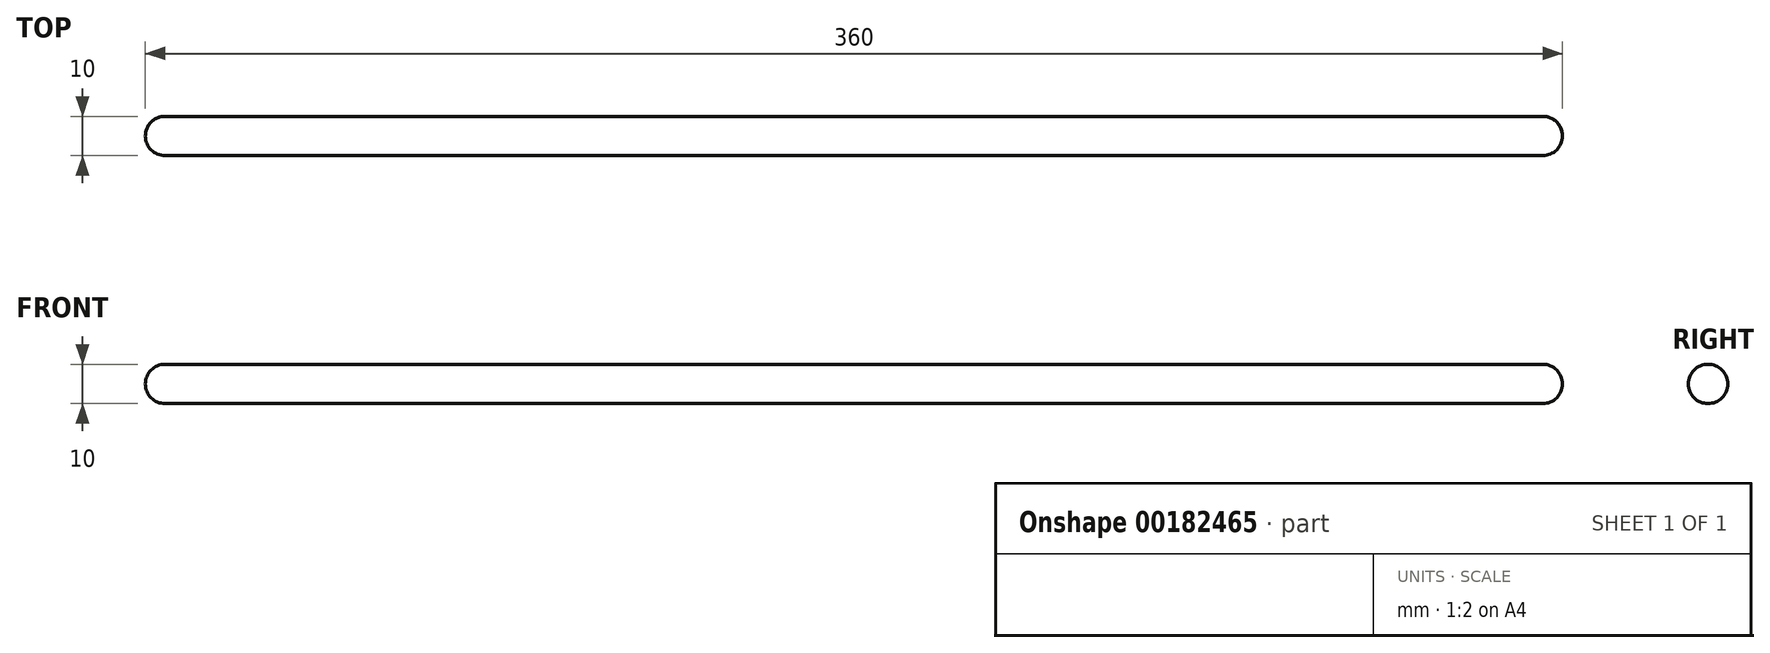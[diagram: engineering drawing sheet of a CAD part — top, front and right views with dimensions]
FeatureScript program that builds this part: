
annotation { "Feature Type Name" : "Feature", "Feature Type Description" : "" }
export const myFeature = defineFeature(function(context is Context, id is Id, definition is map)
    precondition{}
    {
        {
            var Q0;
            Q0=qCreatedBy(makeId("Top.planeOp"),FACE);
            var sketch = newSketch(context, id + "F0", { "sketchPlane" : qUnion([Q0])});
            skLineSegment(sketch, "E0", {"start": v(-153.67, 0) * mm, "end": v(196.33, 0) * mm});
            skCircle(sketch, "E1", {"center": v(-153.67, 0) * mm, "radius": 5 * mm});
            skCircle(sketch, "E2", {"center": v(196.33, 0) * mm, "radius": 5 * mm});
            skLineSegment(sketch, "E3", {"start": v(-153.67, 5) * mm, "end": v(196.33, 5) * mm});
            skLineSegment(sketch, "E4", {"start": v(196.33, -5) * mm, "end": v(-153.67, -5) * mm});
            skLineSegment(sketch, "E5", {"start": v(-153.67, 0) * mm, "end": v(-158.67, 0) * mm});
            skLineSegment(sketch, "E6", {"start": v(196.33, 0) * mm, "end": v(201.33, 0) * mm});
            skSolve(sketch);
        }
        {
            var Q0;
            {var subQ5=sQuery(id+"F0.wireOp",EDGE,"E3");Q0=makeQuery(id+"F0.imprint","IMPRINT",FACE,{"disambiguationData":[TD([[makeQuery(id+"F0.imprint","IMPRINT",EDGE,{"derivedFrom":subQ5}),-1.0]])]});}
            var Q1;
            {var subQ0=sQuery(id+"F0.wireOp",EDGE,"E5");Q1=makeQuery(id+"F0.imprint","IMPRINT",FACE,{"disambiguationData":[TD([[makeQuery(id+"F0.imprint","IMPRINT",EDGE,{"derivedFrom":subQ0}),-1.0]])]});}
            var Q2;
            {var subQ0=sQuery(id+"F0.wireOp",EDGE,"E6");Q2=makeQuery(id+"F0.imprint","IMPRINT",FACE,{"disambiguationData":[TD([[makeQuery(id+"F0.imprint","IMPRINT",EDGE,{"derivedFrom":subQ0}),1.0]])]});}
            var Q3;
            Q3=sQuery(id+"F0.wireOp",EDGE,"E0");
            revolve(context, id + "F1", {"entities" : qUnion([Q0, Q1, Q2]), "axis" : qUnion([Q3]), "revolveType" : RevolveType.FULL});
        }
    });
